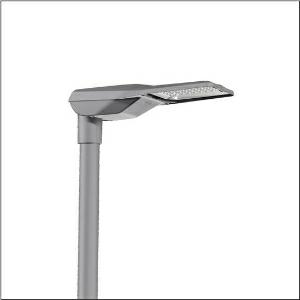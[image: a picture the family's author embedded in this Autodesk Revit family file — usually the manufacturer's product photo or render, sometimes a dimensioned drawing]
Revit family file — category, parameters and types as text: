
# Revit family: streetlight_sl_21_iq_mini___pl52_5xe2h41d08gb_a481
name_source: partatom
category: Lighting Fixtures
units: mm (PartAtom-declared; Revit-internal decimal feet)

## family parameters
Cut with Voids When Loaded = No
Host = Face
Light Source = No
Part Type = Normal
Room Calculation Point = No
Round Connector Dimension = Use Diameter
Shared = No

## types (1)
- --- (1 x LED, 5810 lm, 37.1 W, 4000K)
    Apparent Load = 37 VA
    CIE Flux Codes = 27 59 98 100 100
    Color Rendering = 70
    Color Temperature = 4000K
    Default Elevation = 1800 mm
    Description = Streetlight SL 21 iQ mini, mast luminaire, primary light control with lens, of PMMA, primary optical cover: cover, of toughened safety glass, transparent, light distribution: PL52, light emission: direct distribution, primary light characteristic: asymmetric, installation type: post-top, side-entry, LED, High Power LED, rated luminous flux: 5.810lm, luminous efficacy: 157lm/W, light colour: 740, colour temperature: 4000K, control gear: iQ-Comfort, control: Auto-Match, Temp-Guard, Lumen-Switch, Night-Set, Smart-Wire, Light-Fading, Desk-Remote (wireless, voltage-free reading and setting of iQ features in the workshop via application-optimized NFC function/RFID function), optimised constant luminous flux control (CLO 2.0), pre-setting: linear dimming characteristic, mains connection: 220..240V, AC, 50/60Hz, start of lifetime: 37W, end of service life: 39W, reduction: 18W, luminaire housing, of diecast aluminium, powder-coated, SITECO metallic grey (DB 702S), corrosivity category C5 high according to DIN EN ISO 12944, please order mast flange separately, inclination adjustable: 0°, 5°, 10°, 15°, sealing non-destructively replaceable, multi-level sealing system, length: 628mm, width: 235mm, height: 110mm, mast flange for spigot size: 42mm (side-entry): 5XC10008XM4, 60/48mm (side-entry/post-top): 5XC10108XM2, 76/60mm (side-entry/post-top): 5XC10108XM1, mounting height: 4..8m, protection rating (complete): IP66, insulation class (complete): insulation class II (safety insulation), certification: CE, ENEC, ENEC+, VDE, impact resistance: IK10, permissible operating ambient temperature for outdoor applications: -40..+50°C, standard-compliant lighting for roads and squares, packaging unit: 1 piece

Light Distribution: PL52
    Height = 110 mm
    Lamp = 1 x LED
    Lamp Light Flux = 5810 lm
    Lamp Power = 37.1 W
    Lamp count = 1
    Length = 625 mm
    Luminous efficacy = 157 lm/W
    Manufacturer = Siteco
    ModVariant = No
    Model = 5XE2H41D08GB
    Number of Poles = 1
    OnlyDefault = Yes
    Power Factor = 1
    Product Name = Streetlight SL 21 iQ mini | PL52
    Product group = mast luminaire | pylon top
    ProductGroupID = 6100
    Protection Class = Protection class II
    Protection Degree = IP 66
    RLX_Detail_Level = 1
    RLX_Emergency_Light_Flux = 0 lm
    RLX_Emergency_Type = 0
    RLX_Emergency_Type_DB = No
    RlxData = <blob elided: 36049 chars, md5=1d39d129>
    Socket = socket
    Standby Power = 0 W
    System Light Flux = 5810 lm
    System Power = 37 W
    Type Comments = factory setting: luminous flux: 100 % | dim-lin: 254 | 385 mA
    Type Image = l_1003519.jpg
    URL = http://relux.com
    VarID = @adj_187745
    Voltage = 0 V
    Weight = 0.00 kg
    Width = 234 mm

## geometry (parser evidence)
native form markers: Blend x4, Sweep x9
no freeform markers — native parametric forms only
